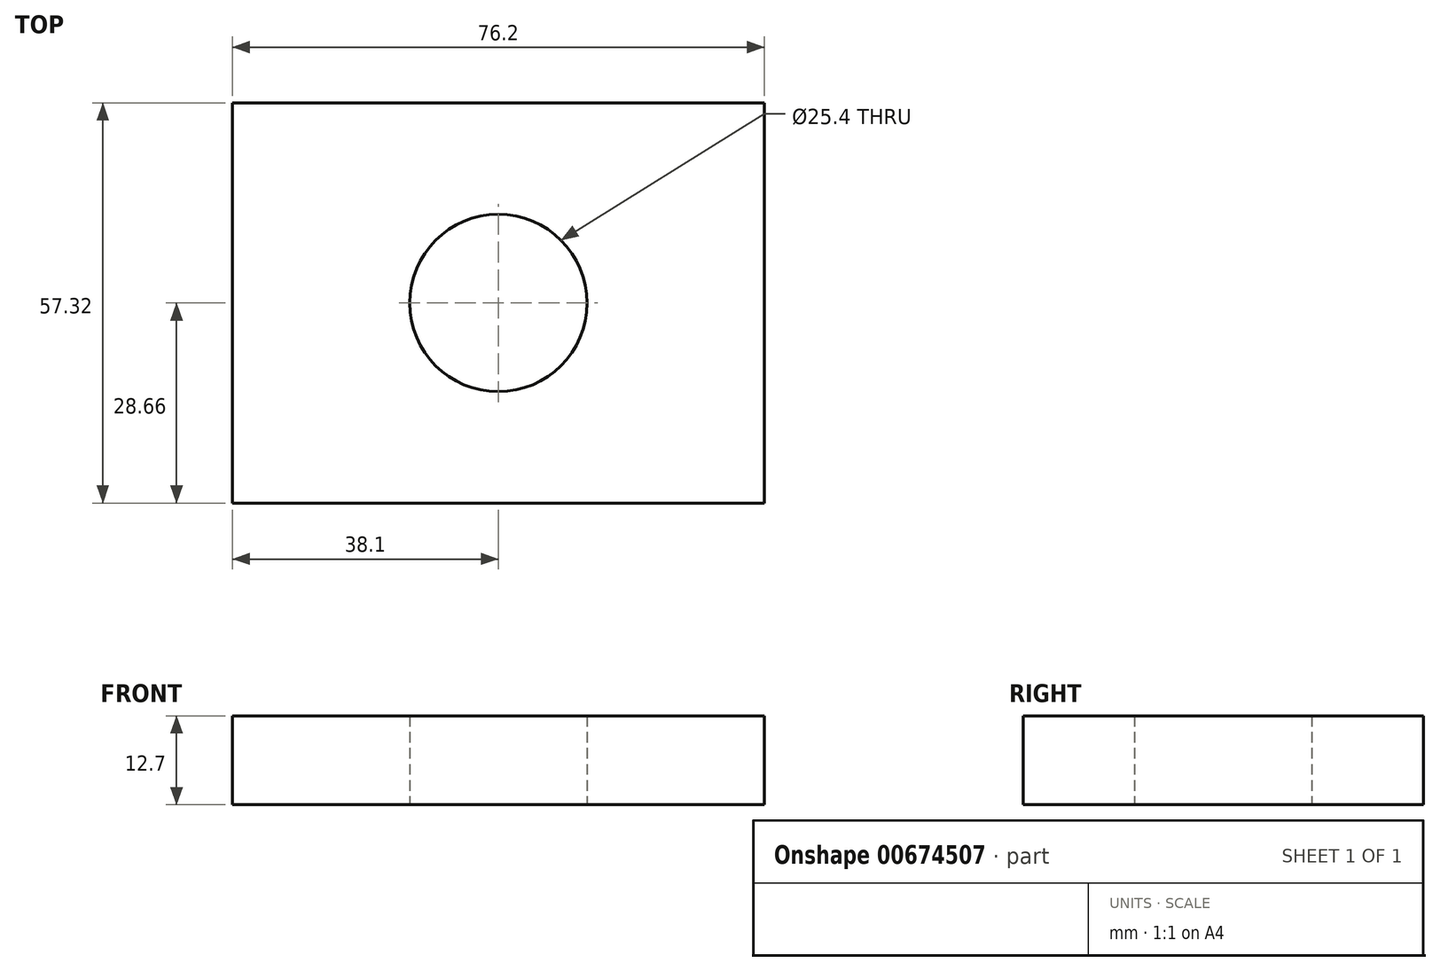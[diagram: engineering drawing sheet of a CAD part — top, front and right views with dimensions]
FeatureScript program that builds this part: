
annotation { "Feature Type Name" : "Feature", "Feature Type Description" : "" }
export const myFeature = defineFeature(function(context is Context, id is Id, definition is map)
    precondition{}
    {
        {
            var Q0;
            Q0=qCreatedBy(makeId("Top.planeOp"),FACE);
            var sketch = newSketch(context, id + "F0", { "sketchPlane" : qUnion([Q0])});
            skLineSegment(sketch, "E0.bottom", {"start": v(38.1, -28.66) * mm, "end": v(-38.1, -28.66) * mm});
            skLineSegment(sketch, "E0.top", {"start": v(38.1, 28.66) * mm, "end": v(-38.1, 28.66) * mm});
            skLineSegment(sketch, "E0.left", {"start": v(38.1, -28.66) * mm, "end": v(38.1, 28.66) * mm});
            skLineSegment(sketch, "E0.right", {"start": v(-38.1, -28.66) * mm, "end": v(-38.1, 28.66) * mm});
            skPoint(sketch, "E0.middle", {"position": v(0, 0) * mm});
            skCircle(sketch, "E1", {"center": v(0, 0) * mm, "radius": 12.7 * mm});
            skSolve(sketch);
        }
        {
            var Q0;
            Q0=makeQuery(id+"F0.imprint","IMPRINT",FACE,{"disambiguationData":[TD([[makeQuery(id+"F0.imprint","IMPRINT",EDGE,{"derivedFrom":sQuery(id+"F0.wireOp",EDGE,"E0.bottom")}),-1.0]])]});
            extrude(context, id + "F1", {"entities" : qUnion([Q0]), "depth" : 12.7 * mm, "offsetDistance" : 25 * mm});
        }
    });
